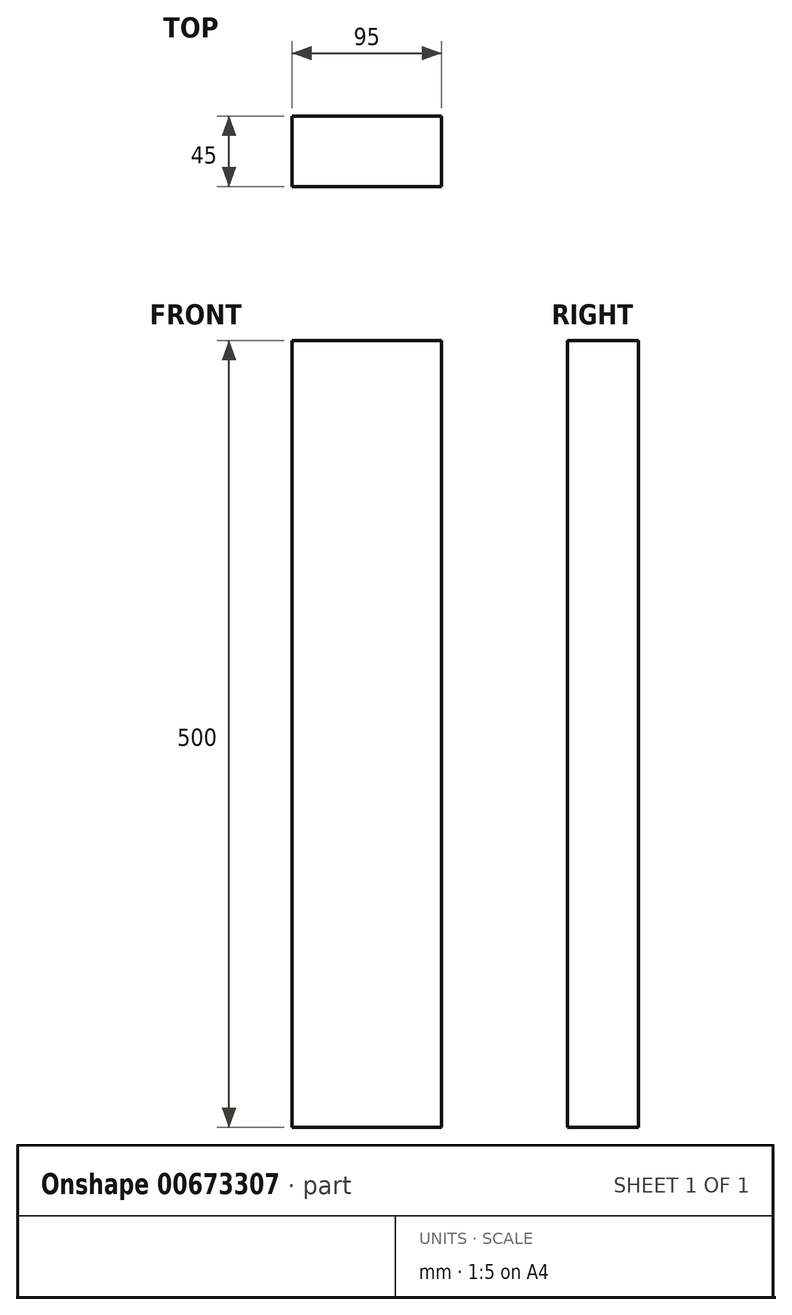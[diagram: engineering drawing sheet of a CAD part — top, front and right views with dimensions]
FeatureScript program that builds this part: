
annotation { "Feature Type Name" : "Feature", "Feature Type Description" : "" }
export const myFeature = defineFeature(function(context is Context, id is Id, definition is map)
    precondition{}
    {
        {
            var Q0;
            Q0=qCreatedBy(makeId("Top.planeOp"),FACE);
            var sketch = newSketch(context, id + "F0", { "sketchPlane" : qUnion([Q0])});
            skLineSegment(sketch, "E0.bottom", {"start": v(0, 0) * mm, "end": v(95, 0) * mm});
            skLineSegment(sketch, "E0.top", {"start": v(0, 45) * mm, "end": v(95, 45) * mm});
            skLineSegment(sketch, "E0.left", {"start": v(0, 0) * mm, "end": v(0, 45) * mm});
            skLineSegment(sketch, "E0.right", {"start": v(95, 0) * mm, "end": v(95, 45) * mm});
            skSolve(sketch);
        }
        {
            var Q0;
            Q0=qSketchRegion(id+"F0",true);
            extrude(context, id + "F1", {"entities" : qUnion([Q0]), "depth" : (750 - 2 * 125) * mm, "offsetDistance" : 25 * mm});
        }
    });
